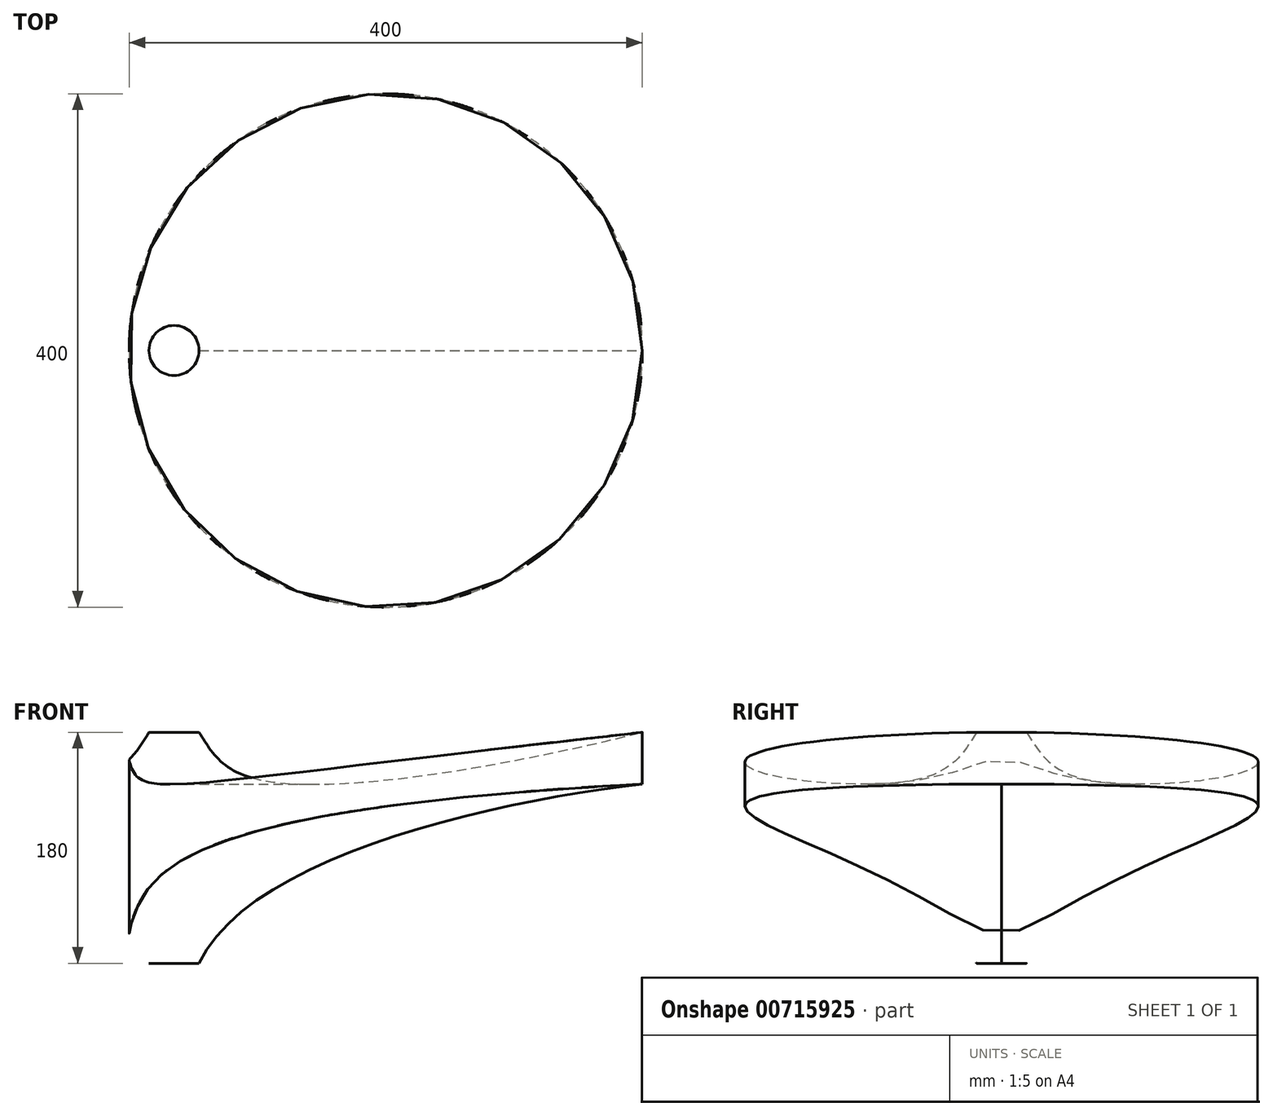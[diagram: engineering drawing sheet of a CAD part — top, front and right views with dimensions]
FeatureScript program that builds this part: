
annotation { "Feature Type Name" : "Feature", "Feature Type Description" : "" }
export const myFeature = defineFeature(function(context is Context, id is Id, definition is map)
    precondition{}
    {
        {
            var Q0;
            Q0=qCreatedBy(makeId("Top.planeOp"),FACE);
            var sketch = newSketch(context, id + "F0", { "sketchPlane" : qUnion([Q0])});
            skCircle(sketch, "E0", {"center": v(165, 0) * mm, "radius": 200 * mm});
            skSolve(sketch);
        }
        {
            var Q0;
            Q0=qCreatedBy(makeId("Front.planeOp"),FACE);
            var sketch = newSketch(context, id + "F1", { "sketchPlane" : qUnion([Q0])});
            skLineSegment(sketch, "E1.bottom", {"start": v(-35, 30) * mm, "end": v(365, 30) * mm, "construction": true});
            skLineSegment(sketch, "E1.top", {"start": v(-35, -150) * mm, "end": v(365, -150) * mm, "construction": true});
            skLineSegment(sketch, "E1.left", {"start": v(-35, 30) * mm, "end": v(-35, -150) * mm, "construction": true});
            skLineSegment(sketch, "E1.right", {"start": v(365, 30) * mm, "end": v(365, -150) * mm, "construction": true});
            skLineSegment(sketch, "E2.bottom", {"start": v(14.5, 187.6) * mm, "end": v(-14.5, 187.6) * mm, "construction": true});
            skLineSegment(sketch, "E2.top", {"start": v(14.5, -412.4) * mm, "end": v(-14.5, -412.4) * mm, "construction": true});
            skLineSegment(sketch, "E2.left", {"start": v(14.5, 187.6) * mm, "end": v(14.5, -412.4) * mm, "construction": true});
            skLineSegment(sketch, "E2.right", {"start": v(-14.5, 187.6) * mm, "end": v(-14.5, -412.4) * mm, "construction": true});
            skPoint(sketch, "E2.middle", {"position": v(0, -112.4) * mm});
            skSolve(sketch);
        }
        {
            var Q0;
            Q0=qCreatedBy(makeId("Front.planeOp"),FACE);
            var sketch = newSketch(context, id + "F2", { "sketchPlane" : qUnion([Q0])});
            skFitSpline(sketch, "E3", {"points": [v(19.5, -150) * mm, v(365, -10.34) * mm], "startDerivative": vector(118.52, 251.85) * mm, "endDerivative": vector(348.27, 40.33) * mm});
            skFitSpline(sketch, "E4", {"points": [v(19.5, 30) * mm, v(58.24, -4.84) * mm, v(365, 30) * mm], "startDerivative": vector(84.15, -132.75) * mm, "endDerivative": vector(439.95, 110.14) * mm});
            skLineSegment(sketch, "E5", {"start": v(365, 30) * mm, "end": v(365, -10.34) * mm});
            skLineSegment(sketch, "E6", {"start": v(19.5, 30) * mm, "end": v(0, 30) * mm});
            skLineSegment(sketch, "E7", {"start": v(0, 30) * mm, "end": v(0, -150) * mm});
            skLineSegment(sketch, "E8", {"start": v(0, -150) * mm, "end": v(19.5, -150) * mm});
            skSolve(sketch);
        }
        {
            var Q0;
            Q0 = qSketchRegion(id + "F2", true);
            var Q1;
            Q1=sQuery(id+"F2.wireOp",EDGE,"E7");
            revolve(context, id + "F3", {"surfaceOperationType" : NewSurfaceOperationType.NEW, "entities" : qUnion([Q0]), "axis" : qUnion([Q1]), "revolveType" : RevolveType.FULL, "oppositeDirection" : true});
        }
        {
            var Q0;
            Q0=makeQuery(id+"F0.imprint","IMPRINT",FACE,{"disambiguationData":[TD([[makeQuery(id+"F0.imprint","IMPRINT",EDGE,{"derivedFrom":sQuery(id+"F0.wireOp",EDGE,"E0")}),1.0]])]});
            var Q1;
            Q1=sQuery(id+"F0.wireOp",EDGE,"E0");
            extrude(context, id + "F4", {"entities" : qUnion([Q0]), "operationType" : NewBodyOperationType.INTERSECT, "surfaceEntities" : qUnion([Q1]), "depth" : 30 * mm, "offsetDistance" : 25 * mm, "hasSecondDirection" : true, "secondDirectionOppositeDirection" : true, "secondDirectionDepth" : 150 * mm});
        }
    });
